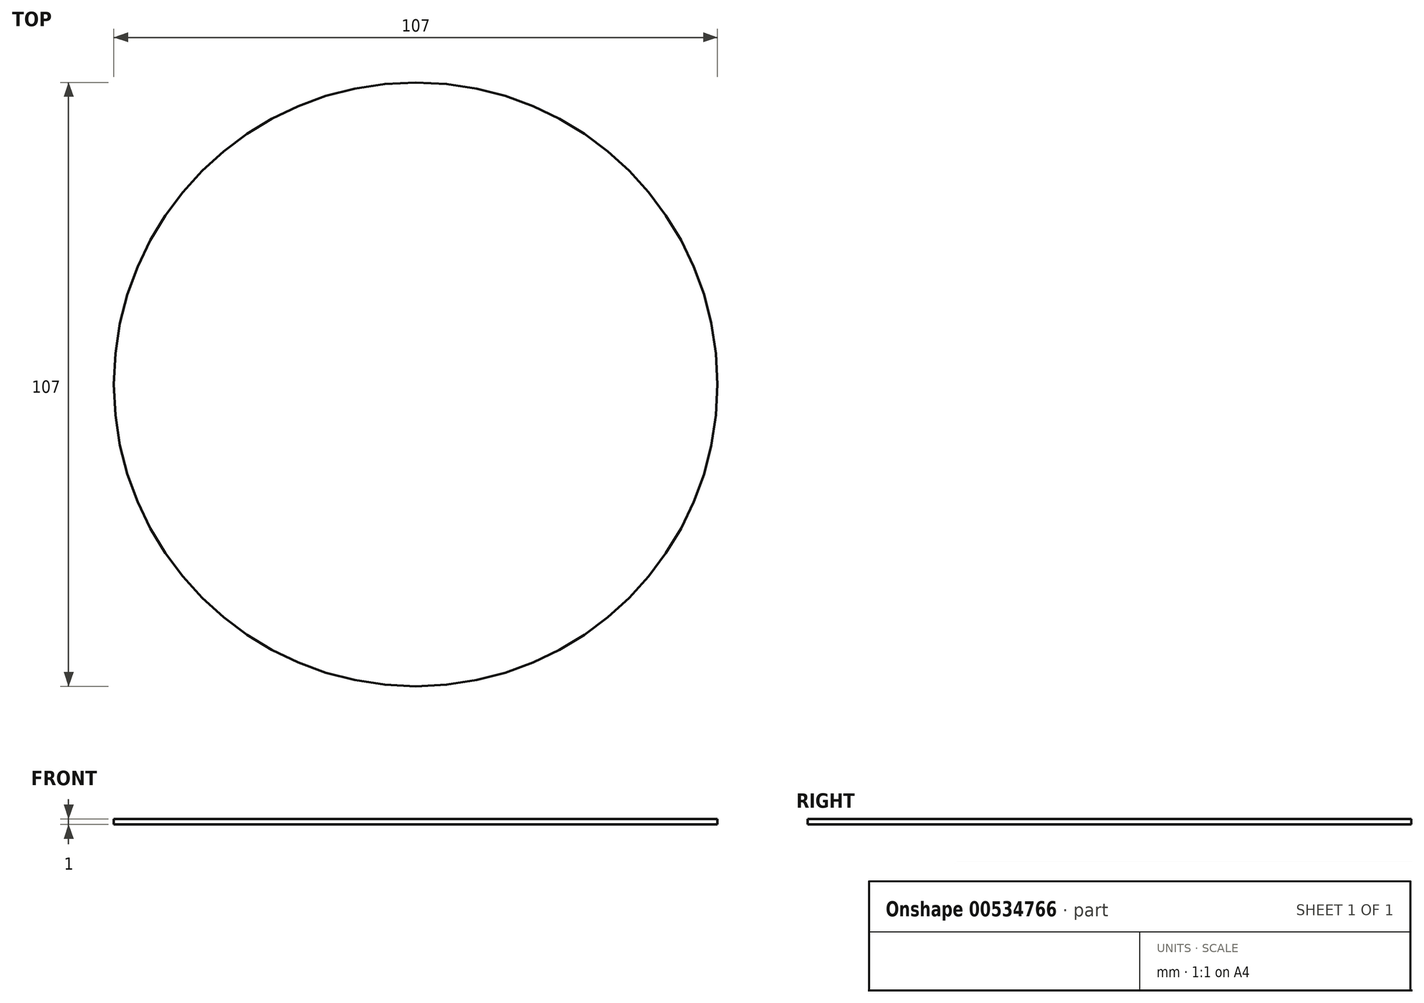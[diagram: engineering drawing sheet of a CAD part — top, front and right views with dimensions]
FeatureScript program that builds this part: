
annotation { "Feature Type Name" : "Feature", "Feature Type Description" : "" }
export const myFeature = defineFeature(function(context is Context, id is Id, definition is map)
    precondition{}
    {
        {
            var Q0;
            Q0=qCreatedBy(makeId("Top.planeOp"),FACE);
            var sketch = newSketch(context, id + "F0", { "sketchPlane" : qUnion([Q0])});
            skLineSegment(sketch, "E0", {"start": v(-75.2, 75.2) * mm, "end": v(76.3, 75.2) * mm});
            skLineSegment(sketch, "E1", {"start": v(75.75, 78.25) * mm, "end": v(75.75, -75.75) * mm});
            skLineSegment(sketch, "E2", {"start": v(75.75, -75.75) * mm, "end": v(-75.75, -75.75) * mm});
            skLineSegment(sketch, "E3", {"start": v(-75.75, -75.75) * mm, "end": v(-75.75, 75.75) * mm});
            skEllipse(sketch, "E4", {"center": v(0, 0) * mm, "majorRadius": 53.5 * mm, "minorRadius": 53.5 * mm, "majorAxis": v(-1, 0)});
            skSolve(sketch);
        }
        {
            var Q0;
            Q0 = qSketchRegion(id + "F0", true);
            var Q1;
            Q1=makeQuery(id+"F0.imprint","IMPRINT",FACE,{"disambiguationData":[TD([[makeQuery(id+"F0.imprint","IMPRINT",EDGE,{"derivedFrom":sQuery(id+"F0.wireOp",EDGE,"393493e9-315b-429e-9538-d358ab09b1fb")}),1.0]])]});
            extrude(context, id + "F1", {"entities" : qUnion([Q0, Q1]), "depth" : 1 * mm, "offsetDistance" : 25 * mm});
        }
    });
